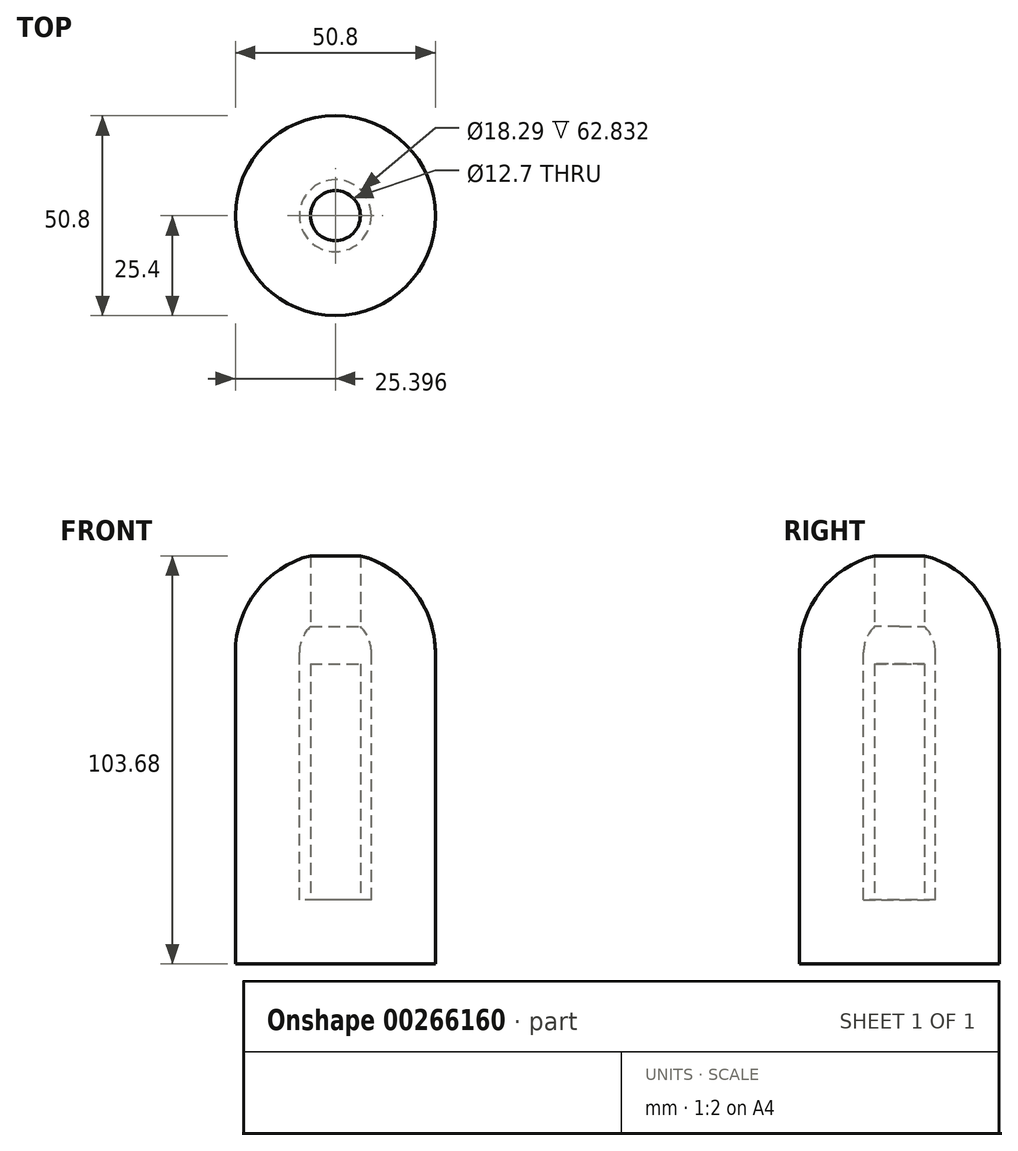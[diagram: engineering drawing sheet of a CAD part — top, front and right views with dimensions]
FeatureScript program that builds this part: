
annotation { "Feature Type Name" : "Feature", "Feature Type Description" : "" }
export const myFeature = defineFeature(function(context is Context, id is Id, definition is map)
    precondition{}
    {
        {
            var Q0;
            Q0=qCreatedBy(makeId("Front.planeOp"),FACE);
            var sketch = newSketch(context, id + "F0", { "sketchPlane" : qUnion([Q0])});
            skLineSegment(sketch, "E0", {"start": v(-3.13, -50.05) * mm, "end": v(22.27, -50.05) * mm});
            skLineSegment(sketch, "E1", {"start": v(22.27, -50.05) * mm, "end": v(22.27, 29.04) * mm});
            skArc(sketch, "E2", {"start": v(22.27, 29.04) * mm, "mid": v(14.83, 47) * mm, "end": v(-3.13, 54.44) * mm});
            skArc(sketch, "E3.0", {"start": v(6, 29.04) * mm, "mid": v(3.33, 35.5) * mm, "end": v(-3.13, 38.18) * mm});
            skLineSegment(sketch, "E3.1", {"start": v(6, -33.8) * mm, "end": v(6, 29.04) * mm});
            skLineSegment(sketch, "E3.2", {"start": v(-3.13, -33.8) * mm, "end": v(6, -33.8) * mm});
            skLineSegment(sketch, "E4", {"start": v(-3.13, 54.44) * mm, "end": v(-3.13, -50.05) * mm});
            skSolve(sketch);
        }
        {
            var Q0;
            {var subQ3=sQuery(id+"F0.wireOp",EDGE,"E0");Q0=makeQuery(id+"F0.imprint","IMPRINT",FACE,{"disambiguationData":[TD([[makeQuery(id+"F0.imprint","IMPRINT",EDGE,{"derivedFrom":subQ3}),1.0]])]});}
            var Q1;
            Q1=sQuery(id+"F0.wireOp",EDGE,"E4");
            revolve(context, id + "F1", {"entities" : qUnion([Q0]), "axis" : qUnion([Q1]), "revolveType" : RevolveType.FULL});
        }
        {
            var Q0;
            Q0=makeQuery(id+"F1.opRevolve","SWEPT_FACE",FACE,{"disambiguationData":[OSD([sQuery(id+"F0.wireOp",EDGE,"E0")])]});
            var sketch = newSketch(context, id + "F2", { "sketchPlane" : qUnion([Q0])});
            skCircle(sketch, "E5", {"center": v(-3.13, 0) * mm, "radius": 6.35 * mm});
            skSolve(sketch);
        }
        {
            var Q0;
            Q0 = qSketchRegion(id + "F2", true);
            extrude(context, id + "F3", {"entities" : qUnion([Q0]), "operationType" : NewBodyOperationType.REMOVE, "endBound" : BoundingType.THROUGH_ALL, "oppositeDirection" : true, "depth" : 25.4 * mm});
        }
        {
            var Q0;
            Q0 = qSketchRegion(id + "F2", true);
            extrude(context, id + "F4", {"entities" : qUnion([Q0]), "operationType" : NewBodyOperationType.ADD, "oppositeDirection" : true, "depth" : 76.2 * mm});
        }
    });
